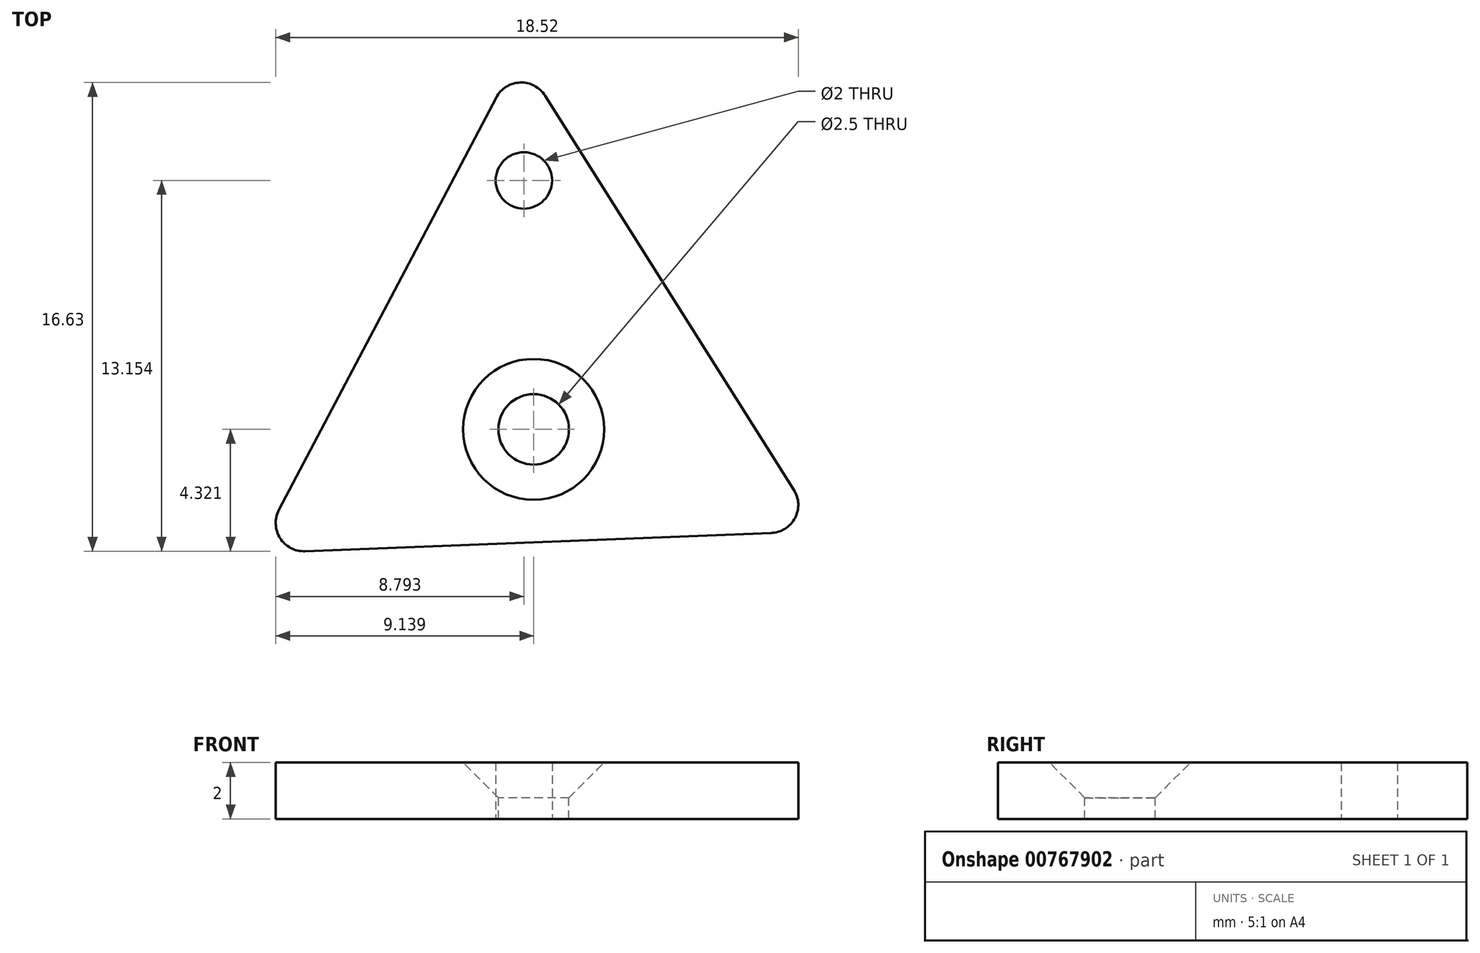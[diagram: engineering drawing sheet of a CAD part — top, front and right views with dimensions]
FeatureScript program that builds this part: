
annotation { "Feature Type Name" : "Feature", "Feature Type Description" : "" }
export const myFeature = defineFeature(function(context is Context, id is Id, definition is map)
    precondition{}
    {
        {
            var Q0;
            Q0=qCreatedBy(makeId("Top.planeOp"),FACE);
            var sketch = newSketch(context, id + "F0", { "sketchPlane" : qUnion([Q0])});
            skCircle(sketch, "E0.cCircle", {"center": v(0, 0) * mm, "radius": 11.55 * mm, "construction": true});
            skLineSegment(sketch, "E0.0", {"start": v(8.49, -5.45) * mm, "end": v(-8.04, -6.1) * mm});
            skLineSegment(sketch, "E0.1", {"start": v(-8.96, -4.63) * mm, "end": v(-1.26, 10) * mm});
            skLineSegment(sketch, "E0.2", {"start": v(0.47, 10.07) * mm, "end": v(9.3, -3.91) * mm});
            skPoint(sketch, "E1.visualSharp", {"position": v(-9.77, -6.16) * mm});
            skArc(sketch, "E1.filletArc", {"start": v(-8.96, -4.63) * mm, "mid": v(-8.92, -5.63) * mm, "end": v(-8.04, -6.1) * mm});
            skPoint(sketch, "E2.visualSharp", {"position": v(-0.45, 11.54) * mm});
            skArc(sketch, "E2.filletArc", {"start": v(0.47, 10.07) * mm, "mid": v(-0.41, 10.54) * mm, "end": v(-1.26, 10) * mm});
            skPoint(sketch, "E3.visualSharp", {"position": v(10.22, -5.38) * mm});
            skArc(sketch, "E3.filletArc", {"start": v(8.49, -5.45) * mm, "mid": v(9.33, -4.91) * mm, "end": v(9.3, -3.91) * mm});
            skLineSegment(sketch, "E4", {"start": v(-0.45, 11.54) * mm, "end": v(0.38, -9.63) * mm, "construction": true});
            skLineSegment(sketch, "E5", {"start": v(-9.77, -6.16) * mm, "end": v(7.6, 4.79) * mm, "construction": true});
            skLineSegment(sketch, "E6", {"start": v(10.22, -5.38) * mm, "end": v(-8.67, 4.56) * mm, "construction": true});
            skCircle(sketch, "E7", {"center": v(-0.28, 7.06) * mm, "radius": 1 * mm});
            skSolve(sketch);
        }
        {
            var Q0;
            Q0 = qSketchRegion(id + "F0", true);
            extrude(context, id + "F1", {"entities" : qUnion([Q0]), "depth" : 2 * mm, "offsetDistance" : 25 * mm});
        }
        {
            var Q0;
            Q0=makeQuery(id+"F1.opExtrude","CAP_FACE",FACE,{"disambiguationData":[OSD([sQuery(id+"F0.wireOp",EDGE,"E0.0"),sQuery(id+"F0.wireOp",EDGE,"E0.1"),sQuery(id+"F0.wireOp",EDGE,"E0.2"),sQuery(id+"F0.wireOp",EDGE,"E1.filletArc"),sQuery(id+"F0.wireOp",EDGE,"E2.filletArc"),sQuery(id+"F0.wireOp",EDGE,"E3.filletArc"),sQuery(id+"F0.wireOp",EDGE,"E7")])],"isStart":false});
            var sketch = newSketch(context, id + "F2", { "sketchPlane" : qUnion([Q0])});
            skLineSegment(sketch, "E8", {"start": v(-0.28, 7.06) * mm, "end": v(0.23, -5.77) * mm, "construction": true});
            skPoint(sketch, "E9", {"position": v(0.07, -1.77) * mm});
            skSolve(sketch);
        }
        {
            var Q0;
            Q0=sQuery(id+"F2.wireOp",VERTEX,"2ac3c492-293f-4a47-8857-296b23899b36");
            var Q1;
            Q1=sQuery(id+"F2.wireOp",VERTEX,"E9");
            var Q2;
            Q2=makeQuery(id+"F1.opExtrude","SWEPT_BODY",BODY,{"disambiguationData":[OSD([sQuery(id+"F0.wireOp",EDGE,"E0.0"),sQuery(id+"F0.wireOp",EDGE,"E0.1"),sQuery(id+"F0.wireOp",EDGE,"E0.2"),sQuery(id+"F0.wireOp",EDGE,"E1.filletArc"),sQuery(id+"F0.wireOp",EDGE,"E2.filletArc"),sQuery(id+"F0.wireOp",EDGE,"E3.filletArc"),sQuery(id+"F0.wireOp",EDGE,"E7")])]});
            hole(context, id + "F3", {"style" : HoleStyle.C_SINK, "endStyle" : HoleEndStyle.BLIND, "holeDiameter" : 2.5 * mm, "cSinkDiameter" : 5 * mm, "cSinkAngle" : 90 * degree, "majorDiameter" : 6.35 * mm, "holeDepth" : 15.8 * mm, "isTappedThrough" : true, "tappedDepth" : 12 * mm, "tapClearance" : 3, "locations" : qUnion([Q0, Q1]), "scope" : qUnion([Q2])});
        }
    });
